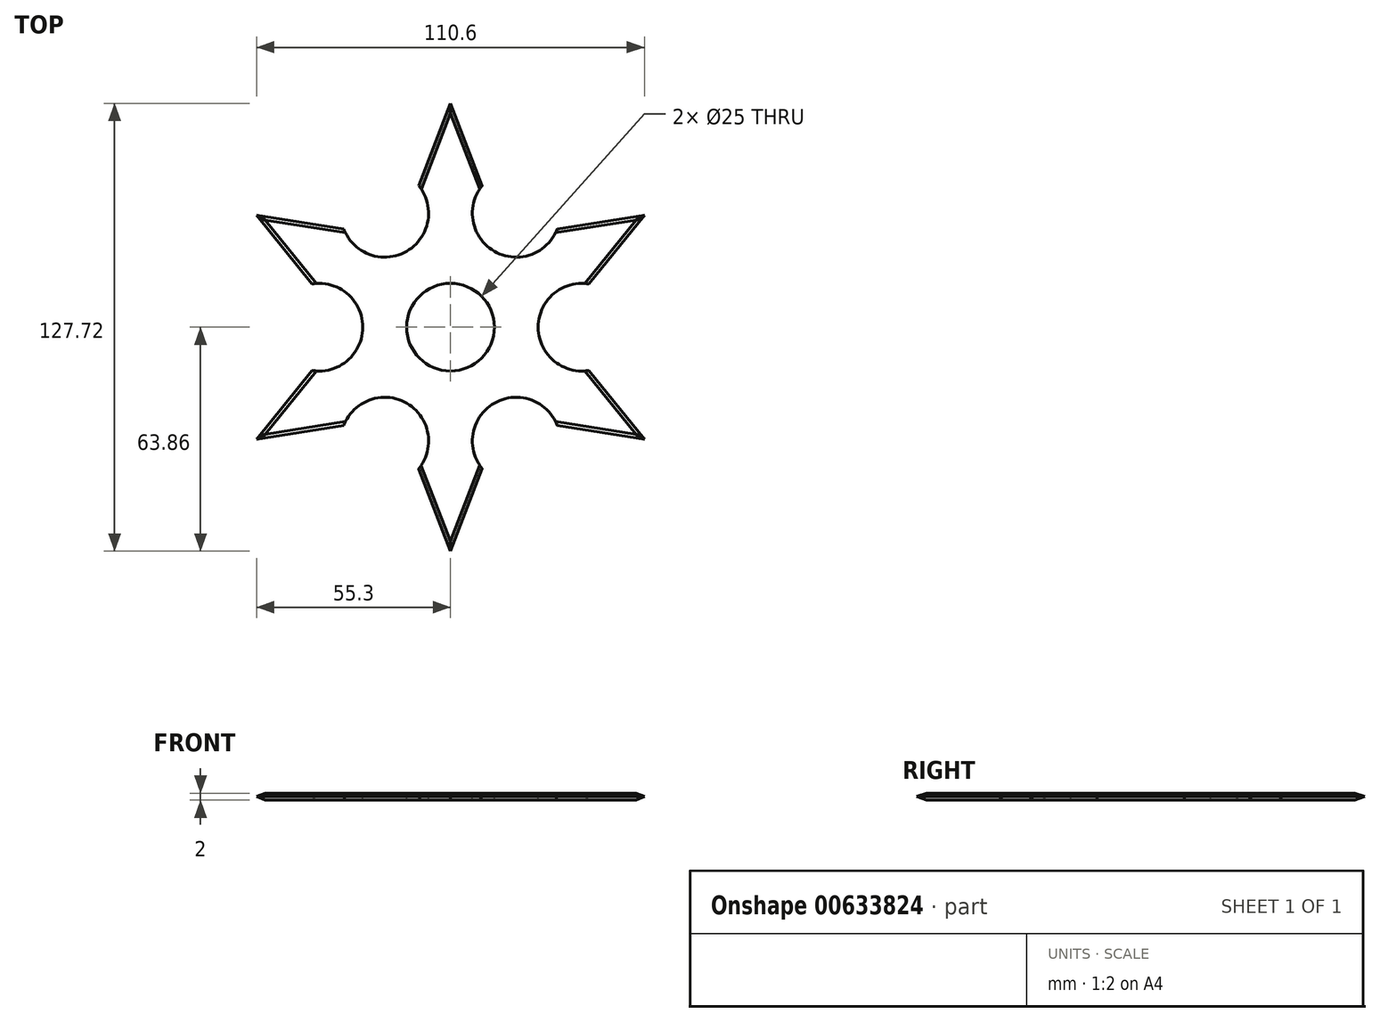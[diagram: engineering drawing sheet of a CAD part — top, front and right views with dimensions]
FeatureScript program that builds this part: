
annotation { "Feature Type Name" : "Feature", "Feature Type Description" : "" }
export const myFeature = defineFeature(function(context is Context, id is Id, definition is map)
    precondition{}
    {
        {
            var Q0;
            Q0=qCreatedBy(makeId("Top.planeOp"),FACE);
            var sketch = newSketch(context, id + "F0", { "sketchPlane" : qUnion([Q0])});
            skCircle(sketch, "E0", {"center": v(0, 0) * mm, "radius": 12.5 * mm});
            skArc(sketch, "E1", {"start": v(31.25, -32.18) * mm, "mid": v(12.53, -21.64) * mm, "end": v(12.2, -43.12) * mm});
            skArc(sketch, "E2", {"start": v(-12.3, -43.18) * mm, "mid": v(-12.47, -21.67) * mm, "end": v(-31.25, -32.18) * mm});
            skArc(sketch, "E3", {"start": v(43.5, 10.97) * mm, "mid": v(25, 0) * mm, "end": v(43.5, -10.97) * mm});
            skArc(sketch, "E4", {"start": v(12.25, 43.15) * mm, "mid": v(12.5, 21.65) * mm, "end": v(31.25, 32.18) * mm});
            skArc(sketch, "E5", {"start": v(-31.25, 32.18) * mm, "mid": v(-12.5, 21.65) * mm, "end": v(-12.25, 43.15) * mm});
            skArc(sketch, "E6", {"start": v(-43.5, -10.97) * mm, "mid": v(-25, 0) * mm, "end": v(-43.5, 10.97) * mm});
            skLineSegment(sketch, "E7", {"start": v(-9.95, -49) * mm, "end": v(-10.05, -49) * mm});
            skPoint(sketch, "E8.end.orphan", {"position": v(0, -66.44) * mm});
            skLineSegment(sketch, "E9", {"start": v(0, -75) * mm, "end": v(9.95, -49) * mm});
            skLineSegment(sketch, "E10", {"start": v(0, -75) * mm, "end": v(-10.05, -49) * mm});
            skPoint(sketch, "E11", {"position": v(43.3, -25) * mm});
            skLineSegment(sketch, "E12", {"start": v(47.41, -15.88) * mm, "end": v(47.44, -15.84) * mm});
            skLineSegment(sketch, "E13", {"start": v(47.44, -15.84) * mm, "end": v(47.41, -15.88) * mm});
            skLineSegment(sketch, "E14", {"start": v(47.44, -15.84) * mm, "end": v(64.95, -37.5) * mm});
            skPoint(sketch, "E15", {"position": v(43.3, 25) * mm});
            skLineSegment(sketch, "E16", {"start": v(37.46, 33.12) * mm, "end": v(37.44, 33.16) * mm});
            skLineSegment(sketch, "E17", {"start": v(47.41, 15.88) * mm, "end": v(47.44, 15.84) * mm});
            skLineSegment(sketch, "E18", {"start": v(64.95, 37.5) * mm, "end": v(47.44, 15.84) * mm});
            skLineSegment(sketch, "E19", {"start": v(64.95, 37.5) * mm, "end": v(37.44, 33.16) * mm});
            skPoint(sketch, "E20", {"position": v(0, 50) * mm});
            skLineSegment(sketch, "E21", {"start": v(9.95, 49) * mm, "end": v(10, 49) * mm});
            skLineSegment(sketch, "E22", {"start": v(-9.95, 49) * mm, "end": v(-10, 49) * mm});
            skLineSegment(sketch, "E23", {"start": v(0, 75) * mm, "end": v(10, 49) * mm});
            skLineSegment(sketch, "E24", {"start": v(0, 75) * mm, "end": v(-10, 49) * mm});
            skPoint(sketch, "E25", {"position": v(-43.3, 25) * mm});
            skLineSegment(sketch, "E26", {"start": v(-37.46, 33.12) * mm, "end": v(-37.44, 33.16) * mm});
            skLineSegment(sketch, "E27", {"start": v(-47.41, 15.88) * mm, "end": v(-47.44, 15.84) * mm});
            skLineSegment(sketch, "E28", {"start": v(-64.95, 37.5) * mm, "end": v(-47.44, 15.84) * mm});
            skLineSegment(sketch, "E29", {"start": v(-64.95, 37.5) * mm, "end": v(-37.44, 33.16) * mm});
            skPoint(sketch, "E30", {"position": v(-43.3, -25) * mm});
            skLineSegment(sketch, "E31", {"start": v(-37.46, -33.12) * mm, "end": v(-37.44, -33.16) * mm});
            skLineSegment(sketch, "E32", {"start": v(-47.41, -15.88) * mm, "end": v(-47.44, -15.84) * mm});
            skLineSegment(sketch, "E33", {"start": v(-64.95, -37.5) * mm, "end": v(-37.44, -33.16) * mm});
            skLineSegment(sketch, "E34", {"start": v(-64.95, -37.5) * mm, "end": v(-47.44, -15.84) * mm});
            skLineSegment(sketch, "E35", {"start": v(10, 49) * mm, "end": v(12.25, 43.15) * mm});
            skLineSegment(sketch, "E36", {"start": v(-10, 49) * mm, "end": v(-12.25, 43.15) * mm});
            skLineSegment(sketch, "E37", {"start": v(-37.44, 33.16) * mm, "end": v(-31.25, 32.18) * mm});
            skLineSegment(sketch, "E38", {"start": v(-47.44, 15.84) * mm, "end": v(-43.5, 10.97) * mm});
            skLineSegment(sketch, "E39", {"start": v(-47.44, -15.84) * mm, "end": v(-43.5, -10.97) * mm});
            skLineSegment(sketch, "E40", {"start": v(-37.44, -33.16) * mm, "end": v(-31.25, -32.18) * mm});
            skLineSegment(sketch, "E41", {"start": v(-10.05, -49) * mm, "end": v(-12.3, -43.18) * mm});
            skLineSegment(sketch, "E42", {"start": v(9.95, -49) * mm, "end": v(12.2, -43.12) * mm});
            skLineSegment(sketch, "E43", {"start": v(47.44, -15.84) * mm, "end": v(43.5, -10.97) * mm});
            skLineSegment(sketch, "E44", {"start": v(47.44, 15.84) * mm, "end": v(43.5, 10.97) * mm});
            skLineSegment(sketch, "E45", {"start": v(37.44, 33.16) * mm, "end": v(31.25, 32.18) * mm});
            skArc(sketch, "E46.trimOffspring", {"start": v(-47.43, -15.83) * mm, "mid": v(-47.42, -15.86) * mm, "end": v(-47.41, -15.88) * mm});
            skArc(sketch, "E47.trimOffspring", {"start": v(-47.41, 15.88) * mm, "mid": v(-47.42, 15.86) * mm, "end": v(-47.43, 15.83) * mm});
            skArc(sketch, "E48.trimOffspring", {"start": v(-9.95, 49) * mm, "mid": v(-9.98, 49) * mm, "end": v(-10, 48.99) * mm});
            skArc(sketch, "E49.trimOffspring", {"start": v(10, 48.99) * mm, "mid": v(9.98, 49) * mm, "end": v(9.95, 49) * mm});
            skArc(sketch, "E50.trimOffspring", {"start": v(37.46, 33.12) * mm, "mid": v(37.44, 33.14) * mm, "end": v(37.42, 33.16) * mm});
            skArc(sketch, "E51.trimOffspring", {"start": v(47.43, 15.83) * mm, "mid": v(47.42, 15.86) * mm, "end": v(47.41, 15.88) * mm});
            skArc(sketch, "E52.trimOffspring", {"start": v(47.41, -15.88) * mm, "mid": v(47.42, -15.86) * mm, "end": v(47.43, -15.83) * mm});
            skArc(sketch, "E53.trimOffspring", {"start": v(-10.06, -48.98) * mm, "mid": v(-10, -48.99) * mm, "end": v(-9.95, -49) * mm});
            skArc(sketch, "E54.trimOffspring", {"start": v(-37.46, -33.12) * mm, "mid": v(-37.44, -33.14) * mm, "end": v(-37.42, -33.16) * mm});
            skLineSegment(sketch, "E55", {"start": v(64.95, -37.5) * mm, "end": v(37.44, -33.16) * mm});
            skLineSegment(sketch, "E56", {"start": v(37.44, -33.16) * mm, "end": v(31.25, -32.18) * mm});
            skSolve(sketch);
        }
        {
            var Q0;
            Q0=makeQuery(id+"F0.imprint","IMPRINT",FACE,{"disambiguationData":[TD([[makeQuery(id+"F0.imprint","IMPRINT",EDGE,{"derivedFrom":sQuery(id+"F0.wireOp",EDGE,"E0")}),-1.0]])]});
            extrude(context, id + "F1", {"entities" : qUnion([Q0]), "depth" : 1 * mm, "offsetDistance" : 25 * mm});
        }
        {
            var Q0;
            Q0=makeQuery(id+"F1.opExtrude","CAP_EDGE",EDGE,{"disambiguationData":[OSD([sQuery(id+"F0.wireOp",EDGE,"E23")])],"isStart":false});
            var Q1;
            Q1=makeQuery(id+"F1.opExtrude","CAP_EDGE",EDGE,{"disambiguationData":[OSD([sQuery(id+"F0.wireOp",EDGE,"E24")])],"isStart":false});
            var Q2;
            Q2=makeQuery(id+"F1.opExtrude","CAP_EDGE",EDGE,{"disambiguationData":[OSD([sQuery(id+"F0.wireOp",EDGE,"E19")])],"isStart":false});
            var Q3;
            Q3=makeQuery(id+"F1.opExtrude","CAP_EDGE",EDGE,{"disambiguationData":[OSD([sQuery(id+"F0.wireOp",EDGE,"E18")])],"isStart":false});
            var Q4;
            Q4=makeQuery(id+"F1.opExtrude","CAP_EDGE",EDGE,{"disambiguationData":[OSD([sQuery(id+"F0.wireOp",EDGE,"E14")])],"isStart":false});
            var Q5;
            Q5=makeQuery(id+"F1.opExtrude","CAP_EDGE",EDGE,{"disambiguationData":[OSD([sQuery(id+"F0.wireOp",EDGE,"Toul9LHT-vnKH-5lqW-PpHv-7WtSMiaRHJ2j")])],"isStart":false});
            var Q6;
            Q6=makeQuery(id+"F1.opExtrude","CAP_EDGE",EDGE,{"disambiguationData":[OSD([sQuery(id+"F0.wireOp",EDGE,"E9"),sQuery(id+"F0.wireOp",EDGE,"E42")])],"isStart":false});
            var Q7;
            Q7=makeQuery(id+"F1.opExtrude","CAP_EDGE",EDGE,{"disambiguationData":[OSD([sQuery(id+"F0.wireOp",EDGE,"E10")])],"isStart":false});
            var Q8;
            Q8=makeQuery(id+"F1.opExtrude","CAP_EDGE",EDGE,{"disambiguationData":[OSD([sQuery(id+"F0.wireOp",EDGE,"E33")])],"isStart":false});
            var Q9;
            Q9=makeQuery(id+"F1.opExtrude","CAP_EDGE",EDGE,{"disambiguationData":[OSD([sQuery(id+"F0.wireOp",EDGE,"E34")])],"isStart":false});
            var Q10;
            Q10=makeQuery(id+"F1.opExtrude","CAP_EDGE",EDGE,{"disambiguationData":[OSD([sQuery(id+"F0.wireOp",EDGE,"E28")])],"isStart":false});
            var Q11;
            Q11=makeQuery(id+"F1.opExtrude","CAP_EDGE",EDGE,{"disambiguationData":[OSD([sQuery(id+"F0.wireOp",EDGE,"E29"),sQuery(id+"F0.wireOp",EDGE,"E37")])],"isStart":false});
            chamfer(context, id + "F2", {"entities" : qUnion([Q0, Q1, Q2, Q3, Q4, Q5, Q6, Q7, Q8, Q9, Q10, Q11]), "width" : 5 * mm, "tangentPropagation" : true});
        }
        {
            var Q0;
            Q0 = qSketchRegion(id + "F0", true);
            extrude(context, id + "F3", {"entities" : qUnion([Q0]), "oppositeDirection" : true, "depth" : 1 * mm, "offsetDistance" : 25 * mm});
        }
        {
            var Q0;
            Q0=makeQuery(id+"F3.opExtrude","CAP_EDGE",EDGE,{"disambiguationData":[OSD([sQuery(id+"F0.wireOp",EDGE,"E24"),sQuery(id+"F0.wireOp",EDGE,"E36")])],"isStart":false});
            var Q1;
            Q1=makeQuery(id+"F3.opExtrude","CAP_EDGE",EDGE,{"disambiguationData":[OSD([sQuery(id+"F0.wireOp",EDGE,"E23"),sQuery(id+"F0.wireOp",EDGE,"E35")])],"isStart":false});
            var Q2;
            Q2=makeQuery(id+"F3.opExtrude","CAP_EDGE",EDGE,{"disambiguationData":[OSD([sQuery(id+"F0.wireOp",EDGE,"E19"),sQuery(id+"F0.wireOp",EDGE,"E45")])],"isStart":false});
            var Q3;
            Q3=makeQuery(id+"F3.opExtrude","CAP_EDGE",EDGE,{"disambiguationData":[OSD([sQuery(id+"F0.wireOp",EDGE,"E18"),sQuery(id+"F0.wireOp",EDGE,"E44")])],"isStart":false});
            var Q4;
            Q4=makeQuery(id+"F3.opExtrude","CAP_EDGE",EDGE,{"disambiguationData":[OSD([sQuery(id+"F0.wireOp",EDGE,"E29"),sQuery(id+"F0.wireOp",EDGE,"E37")])],"isStart":false});
            var Q5;
            Q5=makeQuery(id+"F3.opExtrude","CAP_EDGE",EDGE,{"disambiguationData":[OSD([sQuery(id+"F0.wireOp",EDGE,"E28"),sQuery(id+"F0.wireOp",EDGE,"E38")])],"isStart":false});
            var Q6;
            Q6=makeQuery(id+"F3.opExtrude","CAP_EDGE",EDGE,{"disambiguationData":[OSD([sQuery(id+"F0.wireOp",EDGE,"E34"),sQuery(id+"F0.wireOp",EDGE,"E39")])],"isStart":false});
            var Q7;
            Q7=makeQuery(id+"F3.opExtrude","CAP_EDGE",EDGE,{"disambiguationData":[OSD([sQuery(id+"F0.wireOp",EDGE,"E33"),sQuery(id+"F0.wireOp",EDGE,"E40")])],"isStart":false});
            var Q8;
            Q8=makeQuery(id+"F3.opExtrude","CAP_EDGE",EDGE,{"disambiguationData":[OSD([sQuery(id+"F0.wireOp",EDGE,"E10"),sQuery(id+"F0.wireOp",EDGE,"E41")])],"isStart":false});
            var Q9;
            Q9=makeQuery(id+"F3.opExtrude","CAP_EDGE",EDGE,{"disambiguationData":[OSD([sQuery(id+"F0.wireOp",EDGE,"E9"),sQuery(id+"F0.wireOp",EDGE,"E42")])],"isStart":false});
            chamfer(context, id + "F4", {"entities" : qUnion([Q0, Q1, Q2, Q3, Q4, Q5, Q6, Q7, Q8, Q9]), "width" : 5 * mm, "tangentPropagation" : true});
        }
        {
            var Q0;
            Q0=makeQuery(id+"F3.opExtrude","CAP_EDGE",EDGE,{"disambiguationData":[OSD([sQuery(id+"F0.wireOp",EDGE,"E55"),sQuery(id+"F0.wireOp",EDGE,"E56")])],"isStart":false});
            var Q1;
            Q1=makeQuery(id+"F3.opExtrude","CAP_EDGE",EDGE,{"disambiguationData":[OSD([sQuery(id+"F0.wireOp",EDGE,"E14"),sQuery(id+"F0.wireOp",EDGE,"E43")])],"isStart":false});
            chamfer(context, id + "F5", {"entities" : qUnion([Q0, Q1]), "width" : 5 * mm, "tangentPropagation" : true});
        }
        {
            var Q0;
            Q0=makeQuery(id+"F1.opExtrude","CAP_EDGE",EDGE,{"disambiguationData":[OSD([sQuery(id+"F0.wireOp",EDGE,"E55"),sQuery(id+"F0.wireOp",EDGE,"E56")])],"isStart":false});
            chamfer(context, id + "F6", {"entities" : qUnion([Q0]), "width" : 5 * mm, "tangentPropagation" : true});
        }
    });
